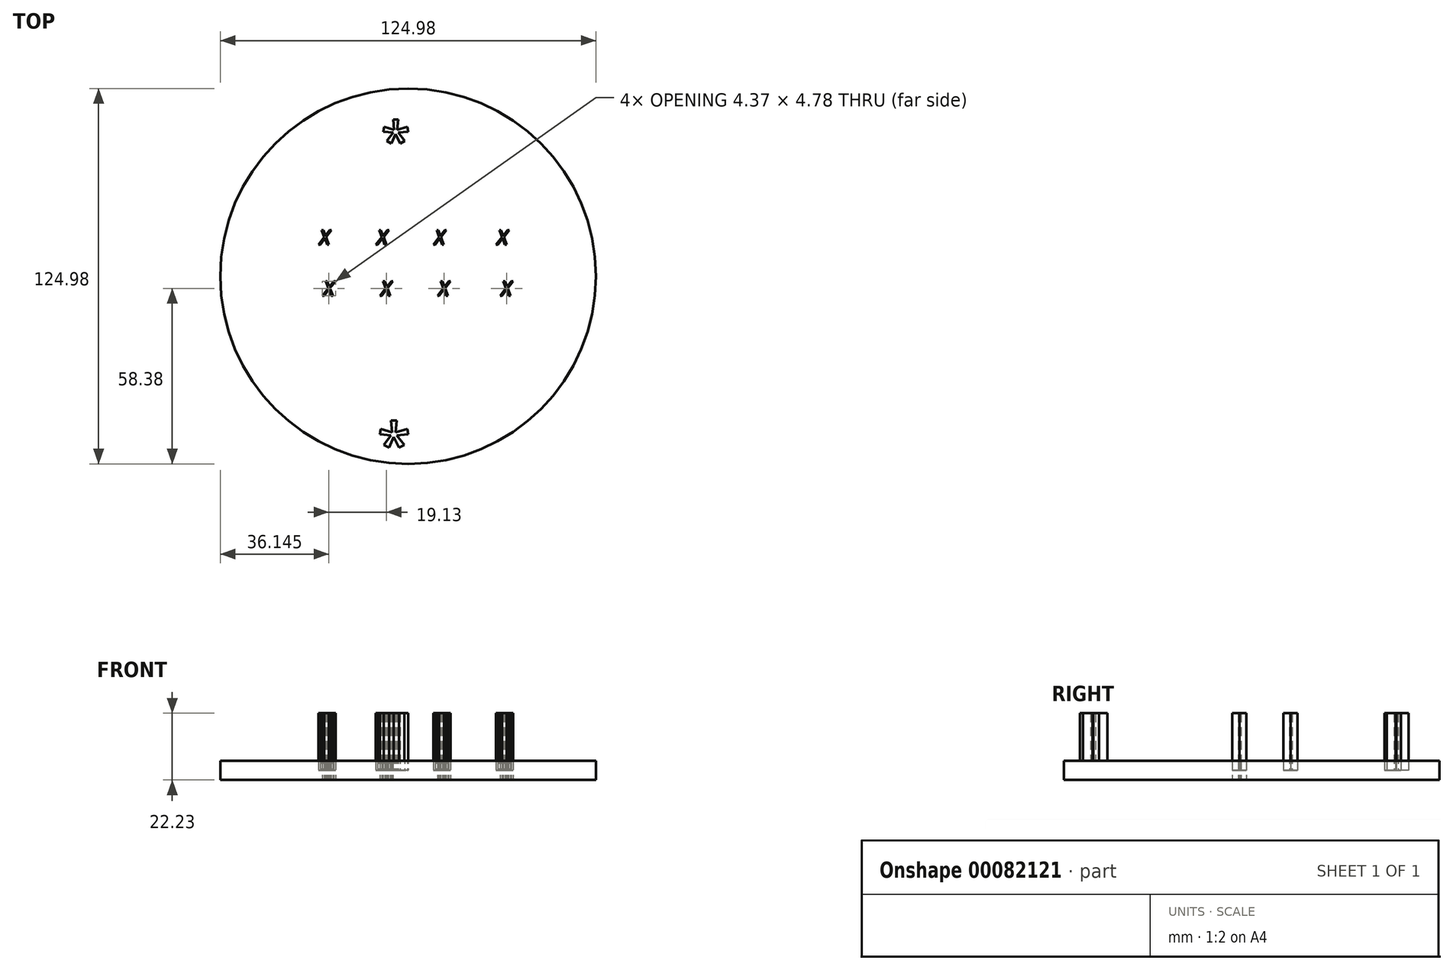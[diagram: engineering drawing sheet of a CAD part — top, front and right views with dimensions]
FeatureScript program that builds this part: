
annotation { "Feature Type Name" : "Feature", "Feature Type Description" : "" }
export const myFeature = defineFeature(function(context is Context, id is Id, definition is map)
    precondition{}
    {
        {
            var Q0;
            Q0=qCreatedBy(makeId("Top.planeOp"),FACE);
            var sketch = newSketch(context, id + "F0", { "sketchPlane" : qUnion([Q0])});
            skCircle(sketch, "E0", {"center": v(0, 0) * mm, "radius": 62.49 * mm});
            skText(sketch, "E1", { "text": "X         X         X          X", "fontName": "OpenSans-Italic.ttf"});
            const initialGuessF0  = {"E1": [-0.02819, -0.0065, 1, 0, 0.00482]};
            skSetInitialGuess(sketch, initialGuessF0);
            skSolve(sketch);
        }
        {
            var Q0;
            Q0=qCreatedBy(makeId("Top.planeOp"),FACE);
            var sketch = newSketch(context, id + "F1", { "sketchPlane" : qUnion([Q0])});
            skText(sketch, "E2", { "text": "*", "fontName": "OpenSans-Regular.ttf"});
            const initialGuessF1  = {"E2": [-0.00902, 0.03866, 1, 0, 0.01281]};
            skSetInitialGuess(sketch, initialGuessF1);
            skSolve(sketch);
        }
        {
            var Q0;
            Q0=qCreatedBy(makeId("Top.planeOp"),FACE);
            var sketch = newSketch(context, id + "F2", { "sketchPlane" : qUnion([Q0])});
            skText(sketch, "E3", { "text": "*", "fontName": "OpenSans-Regular.ttf"});
            const initialGuessF2  = {"E3": [-0.01026, -0.0634, 1, 0, 0.01458]};
            skSetInitialGuess(sketch, initialGuessF2);
            skSolve(sketch);
        }
        {
            var Q0;
            Q0=qCreatedBy(makeId("Top.planeOp"),FACE);
            var sketch = newSketch(context, id + "F3", { "sketchPlane" : qUnion([Q0])});
            skText(sketch, "E4", { "text": "X         X         X          X", "fontName": "OpenSans-Italic.ttf"});
            const initialGuessF3  = {"E4": [-0.02819, -0.0065, 1, 0, 0.00482]};
            skSetInitialGuess(sketch, initialGuessF3);
            skSolve(sketch);
        }
        {
            var Q0;
            Q0=qCreatedBy(makeId("Top.planeOp"),FACE);
            var sketch = newSketch(context, id + "F4", { "sketchPlane" : qUnion([Q0])});
            skText(sketch, "E5", { "text": "X         X         X          X", "fontName": "OpenSans-Italic.ttf"});
            const initialGuessF4  = {"E5": [-0.02951, 0.01051, 1, 0, 0.00482]};
            skSetInitialGuess(sketch, initialGuessF4);
            skSolve(sketch);
        }
        {
            var Q0;
            Q0 = qSketchRegion(id + "F0", true);
            extrude(context, id + "F5", {"entities" : qUnion([Q0]), "endBound" : BoundingType.SYMMETRIC, "depth" : 6.35 * mm});
        }
        {
            var Q0;
            Q0 = qSketchRegion(id + "F1", true);
            extrude(context, id + "F6", {"entities" : qUnion([Q0]), "depth" : 19.05 * mm});
        }
        {
            var Q0;
            Q0 = qSketchRegion(id + "F2", true);
            extrude(context, id + "F7", {"entities" : qUnion([Q0]), "operationType" : NewBodyOperationType.ADD, "depth" : 19.05 * mm});
        }
        {
            var Q0;
            Q0 = qSketchRegion(id + "F3", true);
            extrude(context, id + "F8", {"entities" : qUnion([Q0]), "depth" : 19.05 * mm});
        }
        {
            var Q0;
            Q0 = qSketchRegion(id + "F4", true);
            extrude(context, id + "F9", {"entities" : qUnion([Q0]), "depth" : 19.05 * mm});
        }
        {
            var Q0;
            Q0=qCreatedBy(makeId("Top.planeOp"),FACE);
            var sketch = newSketch(context, id + "F10", { "sketchPlane" : qUnion([Q0])});
            skCircle(sketch, "E6", {"center": v(0, 0) * mm, "radius": 59.93 * mm});
            skSolve(sketch);
        }
        {
            var Q0;
            Q0 = qSketchRegion(id + "F10", true);
            var Q1;
            Q1=sQuery(id+"F10.wireOp",EDGE,"E6");
            extrude(context, id + "F11", {"entities" : qUnion([Q0]), "bodyType" : ToolBodyType.SURFACE, "surfaceEntities" : qUnion([Q1]), "depth" : 6.35 * mm});
        }
    });
